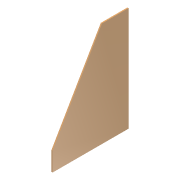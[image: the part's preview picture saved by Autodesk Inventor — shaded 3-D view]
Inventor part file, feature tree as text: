
AUTODESK INVENTOR PART (.ipt)
format: ipt  version: 2014 (Build 180170000, 170)  size: 72,192 bytes
history: native  units: mm
features: extrude x1, sketch x1
ambient origin geometry x8: Origin, YZ Plane, XZ Plane, XY Plane, X Axis, Y Axis, Z Axis, Center Point
bodies: Solid1 (feature_tree)
feature tree (2):
  extrude  "Extrusion1"  Depth=275.0mm
  sketch  "Sketch1"  dims[d0=200.0mm d1=275.0mm d2=70.0mm d3=50.0mm d4=3.0mm d5=0.0mm]
